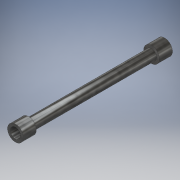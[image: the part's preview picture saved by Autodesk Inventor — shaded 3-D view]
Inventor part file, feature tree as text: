
AUTODESK INVENTOR PART (.ipt)
format: ipt  version: 2018 (Build 220112000, 112)  size: 119,296 bytes
history: native  units: in
note: dims shown in document units (in); Inventor stores cm internally (conversion verified against a paired STEP export)
features: extrude x5, sketch x4
ambient origin geometry x8: Origin, YZ Plane, XZ Plane, XY Plane, X Axis, Y Axis, Z Axis, Center Point
bodies: Solid1 (feature_tree)
feature tree (9):
  extrude  "Extrusion1"  Depth=1.8504in TaperAngle=0.0deg
  sketch  "Sketch2"  dims[d3=0.2362in d4=0.1969in d5=0.0in]
  extrude  "Extrusion2"  Depth=0.1969in TaperAngle=0.0deg
  extrude  "Extrusion3"  Depth=0.1969in TaperAngle=0.0deg
  extrude  "Extrusion4"  Depth=0.1181in TaperAngle=0.0deg
  extrude  "Extrusion5"  [1 undecoded]
  sketch  "Sketch1"  dims[d0=0.1575in d1=1.8504in d2=0.0in]
  sketch  "Sketch3"  dims[d6=0.0787in d7=0.0in d8=0.1969in d9=0.0in]
  sketch  "Sketch4"  dims[d10=0.1575in d11=0.1181in d12=0.0in]
note: 1 required parameter value undecoded (feature->parameter linkage not recoverable at this tier; creation-order binding heuristic only, values carry confidence <= 0.55)
